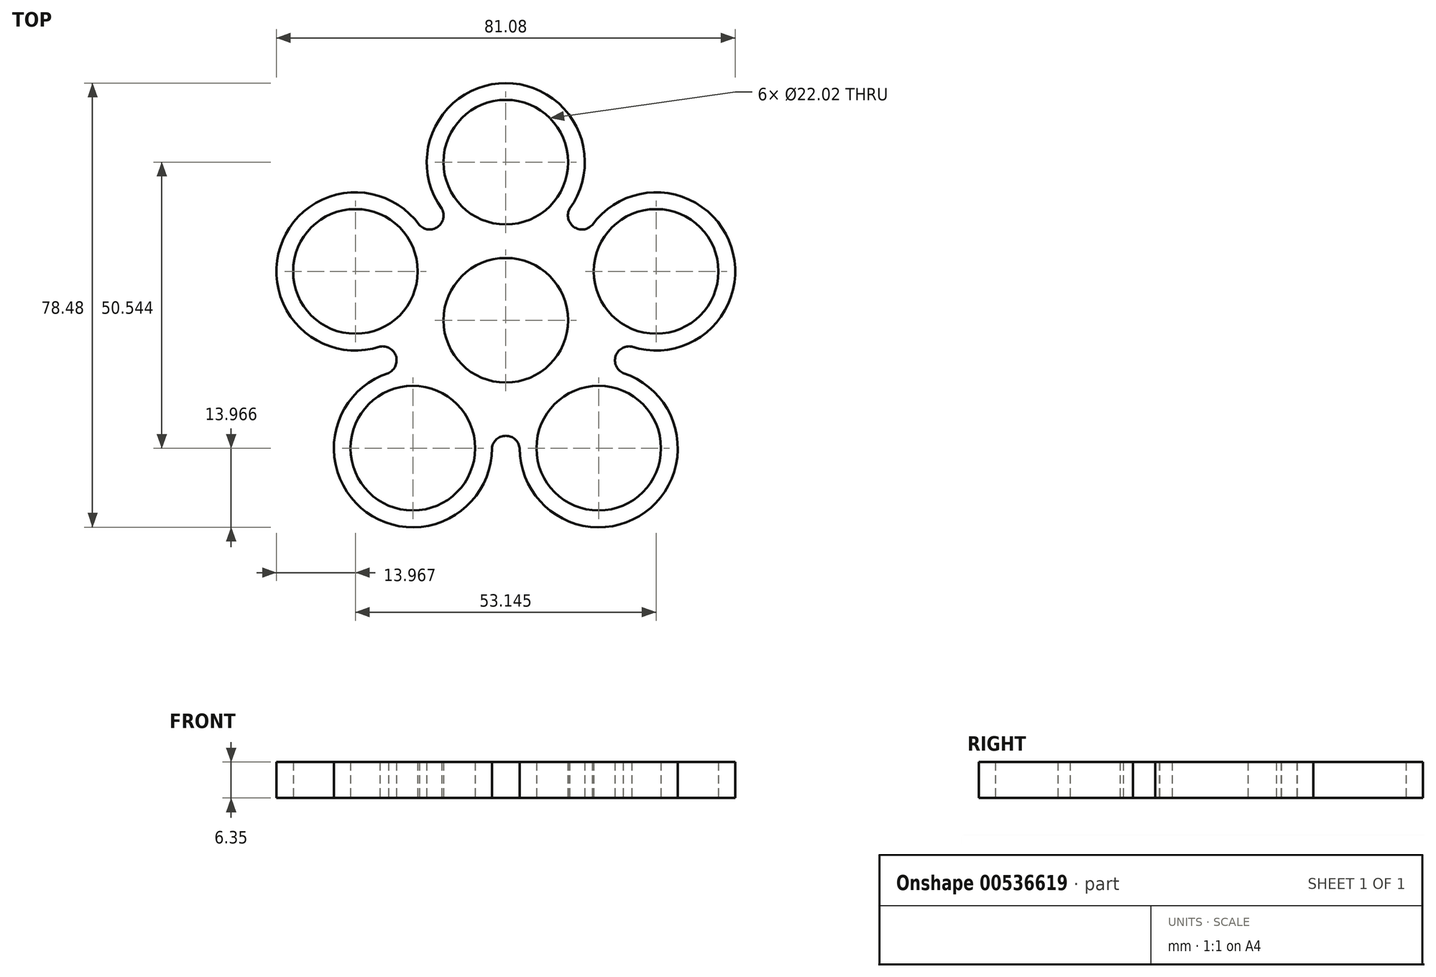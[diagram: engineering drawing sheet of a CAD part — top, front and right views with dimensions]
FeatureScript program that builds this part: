
annotation { "Feature Type Name" : "Feature", "Feature Type Description" : "" }
export const myFeature = defineFeature(function(context is Context, id is Id, definition is map)
    precondition{}
    {
        {
            var Q0;
            Q0=qCreatedBy(makeId("Top.planeOp"),FACE);
            var sketch = newSketch(context, id + "F0", { "sketchPlane" : qUnion([Q0])});
            skCircle(sketch, "E0", {"center": v(0, 0) * mm, "radius": 11.01 * mm});
            skCircle(sketch, "E1", {"center": v(0, 0) * mm, "radius": 13.97 * mm});
            skLineSegment(sketch, "E2", {"start": v(0, 0) * mm, "end": v(0, 27.94) * mm});
            skCircle(sketch, "E3", {"center": v(0, 27.94) * mm, "radius": 11.01 * mm});
            skCircle(sketch, "E4", {"center": v(0, 27.94) * mm, "radius": 13.97 * mm});
            skCircle(sketch, "E5.1.0", {"center": v(-26.57, 8.63) * mm, "radius": 13.97 * mm});
            skCircle(sketch, "E5.2.0", {"center": v(-16.42, -22.6) * mm, "radius": 13.97 * mm});
            skCircle(sketch, "E5.3.0", {"center": v(16.42, -22.6) * mm, "radius": 13.97 * mm});
            skCircle(sketch, "E5.4.0", {"center": v(26.57, 8.63) * mm, "radius": 13.97 * mm});
            skCircle(sketch, "E6.1.0", {"center": v(-26.57, 8.63) * mm, "radius": 11.01 * mm});
            skCircle(sketch, "E6.2.0", {"center": v(-16.42, -22.6) * mm, "radius": 11.01 * mm});
            skCircle(sketch, "E6.3.0", {"center": v(16.42, -22.6) * mm, "radius": 11.01 * mm});
            skCircle(sketch, "E6.4.0", {"center": v(26.57, 8.63) * mm, "radius": 11.01 * mm});
            skSolve(sketch);
        }
        {
            var Q0;
            Q0=makeQuery(id+"F0.imprint","IMPRINT",FACE,{"disambiguationData":[TD([[makeQuery(id+"F0.imprint","IMPRINT",EDGE,{"derivedFrom":sQuery(id+"F0.wireOp",EDGE,"E5.1.0")}),1.0]])]});
            var Q1;
            Q1=makeQuery(id+"F0.imprint","IMPRINT",FACE,{"disambiguationData":[TD([[makeQuery(id+"F0.imprint","IMPRINT",EDGE,{"derivedFrom":sQuery(id+"F0.wireOp",EDGE,"E3")}),-1.0]])]});
            var Q2;
            Q2=makeQuery(id+"F0.imprint","IMPRINT",FACE,{"disambiguationData":[TD([[makeQuery(id+"F0.imprint","IMPRINT",EDGE,{"derivedFrom":sQuery(id+"F0.wireOp",EDGE,"E5.4.0")}),1.0]])]});
            var Q3;
            Q3=makeQuery(id+"F0.imprint","IMPRINT",FACE,{"disambiguationData":[TD([[makeQuery(id+"F0.imprint","IMPRINT",EDGE,{"derivedFrom":sQuery(id+"F0.wireOp",EDGE,"E5.3.0")}),1.0]])]});
            var Q4;
            Q4=makeQuery(id+"F0.imprint","IMPRINT",FACE,{"disambiguationData":[TD([[makeQuery(id+"F0.imprint","IMPRINT",EDGE,{"derivedFrom":sQuery(id+"F0.wireOp",EDGE,"E5.2.0")}),1.0]])]});
            var Q5;
            Q5=makeQuery(id+"F0.imprint","IMPRINT",FACE,{"disambiguationData":[TD([[makeQuery(id+"F0.imprint","IMPRINT",EDGE,{"derivedFrom":sQuery(id+"F0.wireOp",EDGE,"E0")}),-1.0]])]});
            extrude(context, id + "F1", {"entities" : qUnion([Q0, Q1, Q2, Q3, Q4, Q5]), "depth" : 6.35 * mm, "offsetDistance" : 25.4 * mm});
        }
        {
            var Q0;
            Q0=makeQuery(id+"F1.opExtrude","CAP_FACE",FACE,{"disambiguationData":[OSD([sQuery(id+"F0.wireOp",EDGE,"E0"),sQuery(id+"F0.wireOp",EDGE,"E1")])],"isStart":true});
            var sketch = newSketch(context, id + "F2", { "sketchPlane" : qUnion([Q0])});
            skCircle(sketch, "E7.0.0", {"center": v(-16.42, 22.6) * mm, "radius": 13.97 * mm});
            skCircle(sketch, "E8.0.0", {"center": v(-26.57, -8.63) * mm, "radius": 13.97 * mm});
            skCircle(sketch, "E9.0", {"center": v(0, -27.94) * mm, "radius": 13.97 * mm});
            skCircle(sketch, "E10.0", {"center": v(26.57, -8.63) * mm, "radius": 13.97 * mm});
            skCircle(sketch, "E11.0", {"center": v(16.42, 22.6) * mm, "radius": 13.97 * mm});
            skArc(sketch, "E12", {"start": v(-22.26, 4.65) * mm, "mid": v(-19.42, 6.3) * mm, "end": v(-20.74, 9.32) * mm});
            skArc(sketch, "E13.1.0", {"start": v(-11.3, -19.73) * mm, "mid": v(-12, -16.52) * mm, "end": v(-15.27, -16.85) * mm});
            skArc(sketch, "E13.2.0", {"start": v(15.27, -16.85) * mm, "mid": v(12, -16.52) * mm, "end": v(11.3, -19.73) * mm});
            skArc(sketch, "E13.3.0", {"start": v(20.74, 9.32) * mm, "mid": v(19.42, 6.3) * mm, "end": v(22.26, 4.65) * mm});
            skArc(sketch, "E13.4.0", {"start": v(-2.45, 22.6) * mm, "mid": v(0, 20.42) * mm, "end": v(2.45, 22.6) * mm});
            skPoint(sketch, "E13.center", {"position": v(0, 0) * mm});
            skSolve(sketch);
        }
        {
            var Q0;
            {var subQ0=sQuery(id+"F2.wireOp",EDGE,"E13.4.0");Q0=makeQuery(id+"F2.imprint","IMPRINT",FACE,{"disambiguationData":[TD([[makeQuery(id+"F2.imprint","IMPRINT",EDGE,{"derivedFrom":subQ0}),-1.0]])]});}
            var Q1;
            {var subQ0=sQuery(id+"F2.wireOp",EDGE,"E12");Q1=makeQuery(id+"F2.imprint","IMPRINT",FACE,{"disambiguationData":[TD([[makeQuery(id+"F2.imprint","IMPRINT",EDGE,{"derivedFrom":subQ0}),-1.0]])]});}
            var Q2;
            {var subQ0=sQuery(id+"F2.wireOp",EDGE,"E13.1.0");Q2=makeQuery(id+"F2.imprint","IMPRINT",FACE,{"disambiguationData":[TD([[makeQuery(id+"F2.imprint","IMPRINT",EDGE,{"derivedFrom":subQ0}),-1.0]])]});}
            var Q3;
            {var subQ0=sQuery(id+"F2.wireOp",EDGE,"E13.2.0");Q3=makeQuery(id+"F2.imprint","IMPRINT",FACE,{"disambiguationData":[TD([[makeQuery(id+"F2.imprint","IMPRINT",EDGE,{"derivedFrom":subQ0}),-1.0]])]});}
            var Q4;
            {var subQ0=sQuery(id+"F2.wireOp",EDGE,"E13.3.0");Q4=makeQuery(id+"F2.imprint","IMPRINT",FACE,{"disambiguationData":[TD([[makeQuery(id+"F2.imprint","IMPRINT",EDGE,{"derivedFrom":subQ0}),-1.0]])]});}
            extrude(context, id + "F3", {"entities" : qUnion([Q0, Q1, Q2, Q3, Q4]), "operationType" : NewBodyOperationType.ADD, "oppositeDirection" : true, "depth" : 6.35 * mm, "offsetDistance" : 25.4 * mm});
        }
    });
